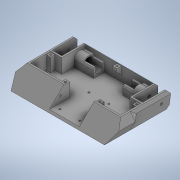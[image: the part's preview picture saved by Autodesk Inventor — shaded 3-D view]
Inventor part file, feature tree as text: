
AUTODESK INVENTOR PART (.ipt)
format: ipt  version: 2020 (Build 240168000, 168)  size: 709,632 bytes
history: native  units: mm
features: extrude x19, sketch x19, projected_geometry x13, chamfer x5, plane x4, mirror x3
ambient origin geometry x8: Origin, YZ Plane, XZ Plane, XY Plane, X Axis, Y Axis, Z Axis, Center Point
bodies: Solid1 (feature_tree)
feature tree (63):
  extrude  "Extrusion1"  Depth=120.0mm
  plane  "Work Plane2"
  extrude  "Extrusion6"  TaperAngle=0.0deg  [1 undecoded]
  chamfer  "Chamfer2"  Distance=83.204mm
  chamfer  "Chamfer3"  Distance=6.0mm Angle=45.0deg
  chamfer  "Chamfer4"  [1 undecoded]
  chamfer  "Chamfer6"  Distance=16.15mm
  extrude  "Extrusion9"  Depth=6.0mm
  extrude  "Extrusion10"  Depth=6.0mm TaperAngle=0.0deg
  extrude  "Extrusion11"  Depth=6.0mm
  extrude  "Extrusion12"  Depth=6.0mm TaperAngle=0.0deg
  mirror  "Mirror2"
  extrude  "WeaponMountSlot"  Depth=10.0mm TaperAngle=0.0deg
  chamfer  "Chamfer7"  Distance=37.4mm
  extrude  "Extrusion14"  Depth=55.8mm
  extrude  "Extrusion15"  Depth=2.0mm TaperAngle=45.0deg
  extrude  "Extrusion16"  Depth=8.0mm
  extrude  "Extrusion17"  Depth=25.5mm
  extrude  "WeaponMountHoles"  TaperAngle=0.0deg  [1 undecoded]
  extrude  "Extrusion19"  Depth=6.0mm
  extrude  "Extrusion20"  Depth=6.0mm
  extrude  "Extrusion21"  Depth=6.0mm
  mirror  "Mirror3"
  extrude  "Extrusion22"  Depth=6.0mm
  plane  "Work Plane7"
  extrude  "Extrusion23"  Depth=7.0mm
  plane  "Work Plane9"
  extrude  "Extrusion27"  TaperAngle=0.0deg  [1 undecoded]
  plane  "Work Plane11"
  extrude  "Extrusion29"  Depth=6.0mm
  mirror  "Mirror6"
  sketch  "Sketch1"  dims[d0=180.0mm d1=120.0mm]
  sketch  "Sketch7"  dims[d2=30.0mm d3=0.0mm]
  projected_geometry  "Projected Loop3"
  sketch  "Sketch11"  dims[d10=45.0deg d18=83.204mm d19=0.0mm]
  projected_geometry  "Projected Loop4"
  sketch  "Sketch12"  dims[d27=3.0mm d28=6.0mm d29=45.0deg]
  projected_geometry  "Projected Loop8"
  sketch  "Sketch16"  dims[d30=24.0mm]
  sketch  "Sketch17"  dims[d31=3.0mm]
  sketch  "Sketch18"  dims[d32=45.0deg]
  sketch  "Sketch19"  dims[d33=3.0mm]
  sketch  "Sketch20"  dims[d34=6.0mm]
  projected_geometry  "Projected Loop9"
  projected_geometry  "Projected Loop10"
  projected_geometry  "Projected Loop11"
  projected_geometry  "Projected Loop12"
  sketch  "Sketch21"  dims[d35=45.0deg]
  sketch  "Sketch22"  dims[d39=24.0mm]
  sketch  "Sketch23"  dims[d40=3.0mm]
  sketch  "Sketch24"  dims[d41=45.0deg]
  sketch  "Sketch25"  dims[d45=17.7mm]
  sketch  "Sketch26"  dims[d46=46.15mm d47=0.0mm d48=0.0mm]
  projected_geometry  "Projected Loop13"
  sketch  "Sketch27"  dims[d52=27.0mm]
  projected_geometry  "Projected Loop14"
  sketch  "Sketch31"  dims[d53=0.0mm]
  projected_geometry  "Projected Loop20"
  projected_geometry  "Projected Loop21"
  sketch  "Sketch37"  dims[d58=6.0mm]
  sketch  "Sketch39"  dims[d64=6.5mm d65=16.15mm d66=15.0mm d67=157.438mm d68=0.0mm d69=4.5mm d70=173.156mm d71=0.0mm d72=10.0mm d73=0.0mm d75=37.4mm d76=55.8mm d77=5.0mm d78=2.0mm d79=45.0deg d80=8.0mm d81=25.5mm d82=0.0mm d83=3.75mm d84=3.75mm d85=3.75mm d86=3.75mm d87=7.0mm d88=0.0mm d90=6.0mm d91=4.0mm d92=15.0mm d93=23.0mm d94=7.0mm d95=0.0mm d96=4.0mm d97=15.0mm d98=23.0mm d99=7.0mm d100=0.0mm d101=3.0mm d102=60.0mm d103=3.1mm d104=3.1mm d105=3.1mm d106=3.1mm d107=10.0mm d108=9.4mm d109=9.4mm d110=64.0mm d111=64.0mm d112=9.4mm d113=9.4mm d114=10.0mm d115=27.0mm d116=0.0mm d117=6.1mm d118=0.0mm d119=-7.853982mm d120=16.3mm d121=16.15mm d122=15.0mm d123=2.0mm d124=20.3mm d125=17.0mm d126=0.0mm d127=15.5mm d128=12.2mm d129=19.0mm d130=0.0mm d131=45.0deg d133=19.0mm d134=0.0mm d135=8.0mm d137=6.1mm d138=3.0mm d139=3.0mm d144=10.0mm d145=0.0mm d148=6.0mm d149=-72.0mm d156=5.0mm d157=0.0mm d161=5.0mm d162=0.0mm d164=8.726646mm]
  projected_geometry  "Project Cut Edges3"
  projected_geometry  "Project Cut Edges4"
note: 4 required parameter values undecoded (feature->parameter linkage not recoverable at this tier; creation-order binding heuristic only, values carry confidence <= 0.55)
